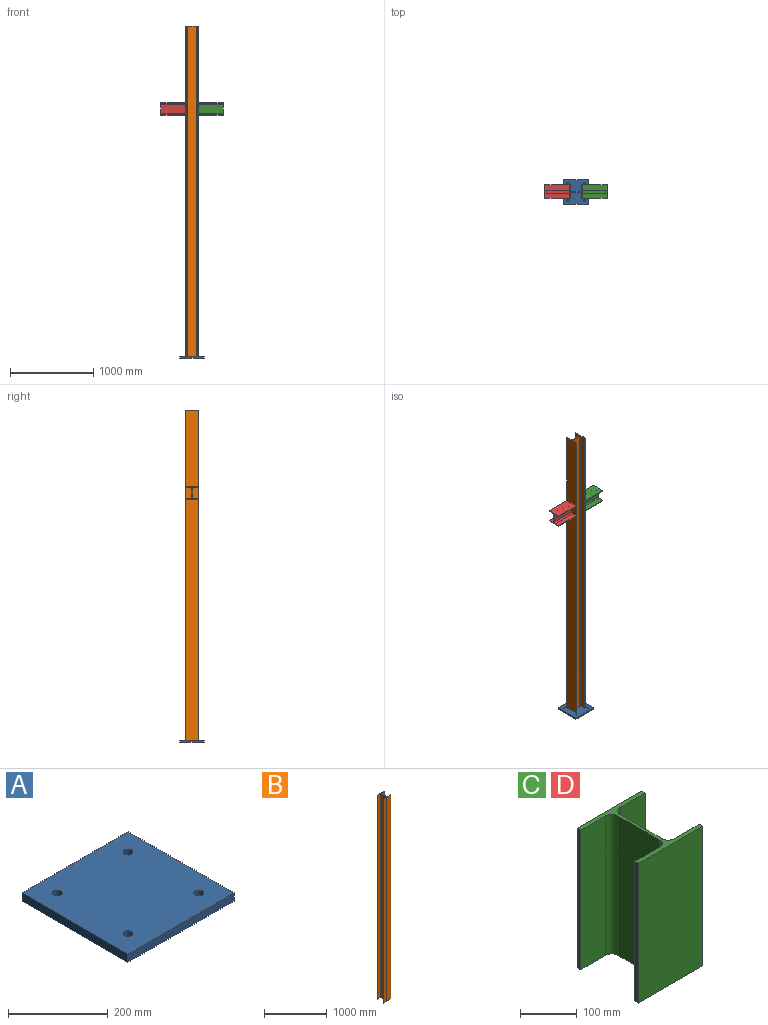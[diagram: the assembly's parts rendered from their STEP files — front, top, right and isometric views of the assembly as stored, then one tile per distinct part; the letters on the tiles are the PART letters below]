
ASSEMBLY  parts=4 mates=3
PART A: 10 faces, bbox 300x300x20 mm
  f0: plane 300x20mm, normal (1,0,0), area 6000mm2, adj f1,f6,f8,f9
  f1: plane 300x20mm, normal (0,1,0), area 6000mm2, adj f0,f2,f8,f9
  f2: plane 300x20mm, normal (-1,0,0), area 6000mm2, adj f1,f6,f8,f9
  f3: cylinder r=10mm len=20mm, axis (0,0,-1), area 1256.6mm2, adj f8,f9
  f4: cylinder r=10mm len=20mm, axis (0,0,-1), area 1256.6mm2, adj f8,f9
  f5: cylinder r=10mm len=20mm, axis (0,0,-1), area 1256.6mm2, adj f8,f9
  f6: plane 300x20mm, normal (0,-1,0), area 6000mm2, adj f0,f2,f8,f9
  f7: cylinder r=10mm len=20mm, axis (0,0,-1), area 1256.6mm2, adj f8,f9
  f8: plane 300x300mm, normal (0,0,1), area 88743.4mm2, adj f0,f1,f2,f3,f4,f5,f6,f7
  f9: plane 300x300mm, normal (0,0,-1), area 88743.4mm2, adj f0,f1,f2,f3,f4,f5,f6,f7
PART B: 18 faces, bbox 160x152x3980 mm
  f0: plane 3980x9mm, normal (-1,0,0), area 35820mm2, adj f1,f15,f16,f17
  f1: plane 3980x62mm, normal (0,1,0), area 246760mm2, adj f0,f2,f16,f17
  f2: cylinder r=15mm len=3980mm, axis (0,0,1), area 93776.5mm2, adj f1,f3,f16,f17
  f3: plane 3980x104mm, normal (-1,0,0), area 413920mm2, adj f2,f4,f16,f17
  f4: cylinder r=15mm len=3980mm, axis (0,0,1), area 93776.5mm2, adj f3,f5,f16,f17
  f5: plane 3980x62mm, normal (0,-1,0), area 246760mm2, adj f4,f6,f16,f17
  f6: plane 3980x9mm, normal (-1,0,0), area 35820mm2, adj f5,f7,f16,f17
  f7: plane 3980x160mm, normal (0,1,0), area 636800mm2, adj f6,f8,f16,f17
  f8: plane 3980x9mm, normal (1,0,0), area 35820mm2, adj f7,f9,f16,f17
  f9: plane 3980x62mm, normal (0,-1,0), area 246760mm2, adj f8,f10,f16,f17
  f10: cylinder r=15mm len=3980mm, axis (0,0,1), area 93776.5mm2, adj f9,f11,f16,f17
  f11: plane 3980x104mm, normal (1,0,0), area 413920mm2, adj f10,f12,f16,f17
  f12: cylinder r=15mm len=3980mm, axis (0,0,1), area 93776.5mm2, adj f11,f13,f16,f17
  f13: plane 3980x62mm, normal (0,1,0), area 246760mm2, adj f12,f14,f16,f17
  f14: plane 3980x9mm, normal (1,0,0), area 35820mm2, adj f13,f15,f16,f17
  f15: plane 3980x160mm, normal (0,-1,0), area 636800mm2, adj f0,f14,f16,f17
  f16: plane 160x152mm, normal (0,0,1), area 3877.1mm2, adj f0,f1,f2,f3,f4,f5,f6,f7
  f17: plane 160x152mm, normal (0,0,-1), area 3877.1mm2, adj f0,f1,f2,f3,f4,f5,f6,f7
PART C: 18 faces, bbox 160x152x300 mm
  f0: plane 300x9mm, normal (-1,0,0), area 2700mm2, adj f1,f15,f16,f17
  f1: plane 300x62mm, normal (0,1,0), area 18600mm2, adj f0,f2,f16,f17
  f2: cylinder r=15mm len=300mm, axis (0,0,1), area 7068.6mm2, adj f1,f3,f16,f17
  f3: plane 300x104mm, normal (-1,0,0), area 31200mm2, adj f2,f4,f16,f17
  f4: cylinder r=15mm len=300mm, axis (0,0,1), area 7068.6mm2, adj f3,f5,f16,f17
  f5: plane 300x62mm, normal (0,-1,0), area 18600mm2, adj f4,f6,f16,f17
  f6: plane 300x9mm, normal (-1,0,0), area 2700mm2, adj f5,f7,f16,f17
  f7: plane 300x160mm, normal (0,1,0), area 48000mm2, adj f6,f8,f16,f17
  f8: plane 300x9mm, normal (1,0,0), area 2700mm2, adj f7,f9,f16,f17
  f9: plane 300x62mm, normal (0,-1,0), area 18600mm2, adj f8,f10,f16,f17
  f10: cylinder r=15mm len=300mm, axis (0,0,1), area 7068.6mm2, adj f9,f11,f16,f17
  f11: plane 300x104mm, normal (1,0,0), area 31200mm2, adj f10,f12,f16,f17
  f12: cylinder r=15mm len=300mm, axis (0,0,1), area 7068.6mm2, adj f11,f13,f16,f17
  f13: plane 300x62mm, normal (0,1,0), area 18600mm2, adj f12,f14,f16,f17
  f14: plane 300x9mm, normal (1,0,0), area 2700mm2, adj f13,f15,f16,f17
  f15: plane 300x160mm, normal (0,-1,0), area 48000mm2, adj f0,f14,f16,f17
  f16: plane 160x152mm, normal (0,0,1), area 3877.1mm2, adj f0,f1,f2,f3,f4,f5,f6,f7
  f17: plane 160x152mm, normal (0,0,-1), area 3877.1mm2, adj f0,f1,f2,f3,f4,f5,f6,f7
PART D: same geometry as C
PLACE A at identity
PLACE B rot(axis=(0,0,1),90deg) t=(0,0,2010)mm
PLACE C rot(axis=(0.58,-0.58,-0.58),120deg) t=(226,0,3000)mm
PLACE D rot(axis=(0.58,-0.58,-0.58),120deg) t=(-226,0,3000)mm
MATE fastened B.f17 <-> A.f8  axis (0,0,-1) through (0,0,20)mm
MATE fastened C.f16 <-> B.f15  axis (-1,0,0) through (76,0,3000)mm
MATE fastened D.f17 <-> B.f7  axis (1,0,0) through (-76,0,3000)mm
